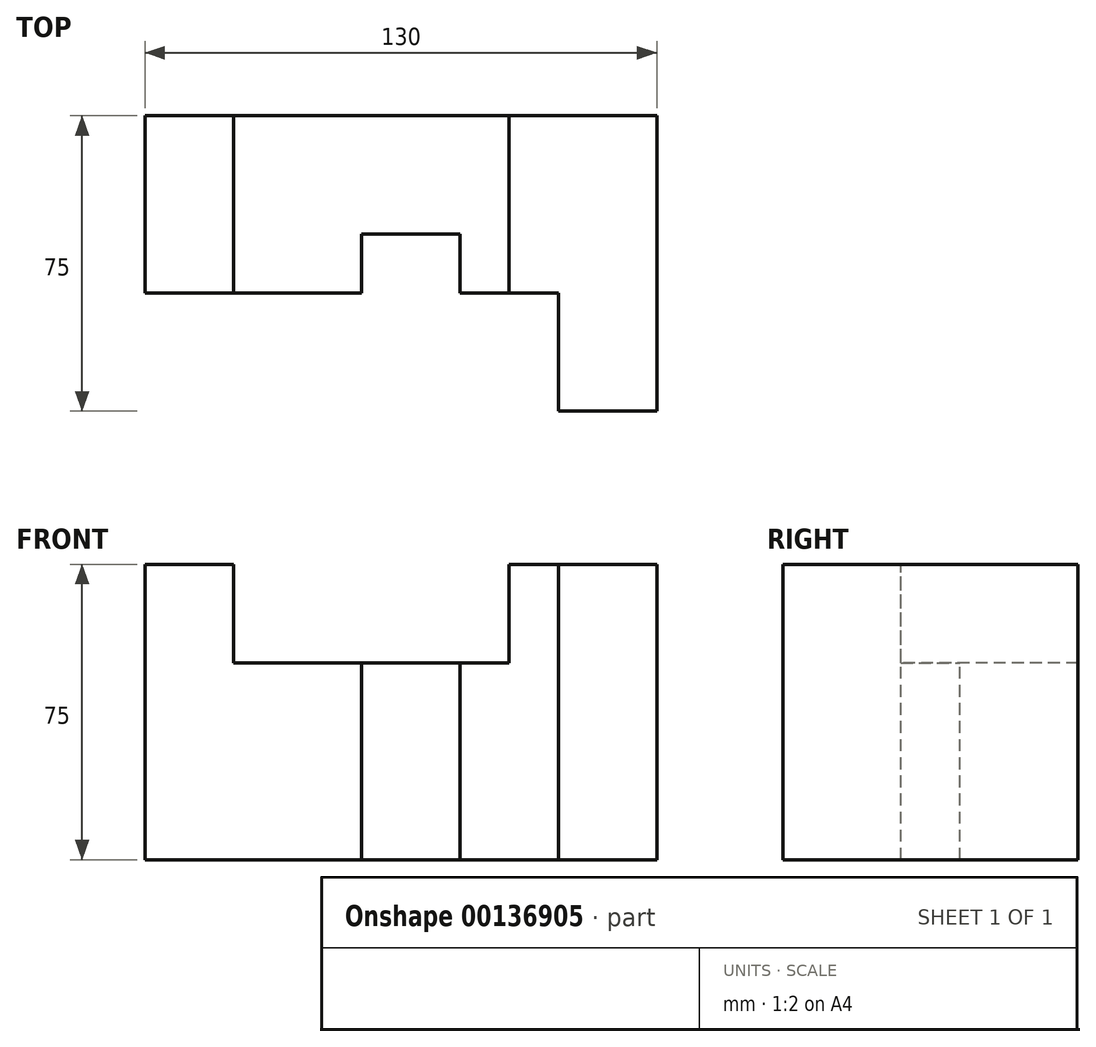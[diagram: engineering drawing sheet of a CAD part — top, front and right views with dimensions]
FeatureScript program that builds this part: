
annotation { "Feature Type Name" : "Feature", "Feature Type Description" : "" }
export const myFeature = defineFeature(function(context is Context, id is Id, definition is map)
    precondition{}
    {
        {
            var Q0;
            Q0=qCreatedBy(makeId("Top.planeOp"),FACE);
            var sketch = newSketch(context, id + "F0", { "sketchPlane" : qUnion([Q0])});
            skLineSegment(sketch, "E0", {"start": v(0, 0) * mm, "end": v(130, 0) * mm});
            skLineSegment(sketch, "E1", {"start": v(130, 0) * mm, "end": v(130, 75) * mm});
            skLineSegment(sketch, "E2", {"start": v(130, 75) * mm, "end": v(0, 75) * mm});
            skLineSegment(sketch, "E3", {"start": v(0, 75) * mm, "end": v(0, 0) * mm});
            skSolve(sketch);
        }
        {
            var Q0;
            Q0 = qSketchRegion(id + "F0", true);
            extrude(context, id + "F1", {"entities" : qUnion([Q0]), "depth" : 75 * mm});
        }
        {
            var Q0;
            Q0=makeQuery(id+"F1.opExtrude","CAP_FACE",FACE,{"disambiguationData":[OSD([sQuery(id+"F0.wireOp",EDGE,"E0"),sQuery(id+"F0.wireOp",EDGE,"E1"),sQuery(id+"F0.wireOp",EDGE,"E2"),sQuery(id+"F0.wireOp",EDGE,"E3")])],"isStart":false});
            var sketch = newSketch(context, id + "F2", { "sketchPlane" : qUnion([Q0])});
            skLineSegment(sketch, "E4", {"start": v(105, 0) * mm, "end": v(105, 30) * mm});
            skLineSegment(sketch, "E5", {"start": v(105, 30) * mm, "end": v(80, 30) * mm});
            skLineSegment(sketch, "E6", {"start": v(80, 30) * mm, "end": v(80, 45) * mm});
            skLineSegment(sketch, "E7", {"start": v(80, 45) * mm, "end": v(55, 45) * mm});
            skLineSegment(sketch, "E8", {"start": v(55, 45) * mm, "end": v(55, 30) * mm});
            skLineSegment(sketch, "E9", {"start": v(55, 30) * mm, "end": v(0, 30) * mm});
            skLineSegment(sketch, "E10", {"start": v(0, 30) * mm, "end": v(0, 0) * mm});
            skLineSegment(sketch, "E11", {"start": v(0, 0) * mm, "end": v(105, 0) * mm});
            skSolve(sketch);
        }
        {
            var Q0;
            Q0 = qSketchRegion(id + "F2", true);
            extrude(context, id + "F3", {"entities" : qUnion([Q0]), "operationType" : NewBodyOperationType.REMOVE, "oppositeDirection" : true, "depth" : 90 * mm});
        }
        {
            var Q0;
            Q0=makeQuery(id+"F1.opExtrude","CAP_FACE",FACE,{"disambiguationData":[OSD([sQuery(id+"F0.wireOp",EDGE,"E0"),sQuery(id+"F0.wireOp",EDGE,"E1"),sQuery(id+"F0.wireOp",EDGE,"E2"),sQuery(id+"F0.wireOp",EDGE,"E3")])],"isStart":false});
            var sketch = newSketch(context, id + "F4", { "sketchPlane" : qUnion([Q0])});
            skLineSegment(sketch, "E12", {"start": v(22.5, 75) * mm, "end": v(22.5, 30) * mm});
            skLineSegment(sketch, "E13", {"start": v(22.5, 30) * mm, "end": v(92.5, 30) * mm});
            skLineSegment(sketch, "E14", {"start": v(92.5, 30) * mm, "end": v(92.5, 75) * mm});
            skLineSegment(sketch, "E15", {"start": v(92.5, 75) * mm, "end": v(22.5, 75) * mm});
            skSolve(sketch);
        }
        {
            var Q0;
            {var subQ4=sQuery(id+"F4.wireOp",EDGE,"E12");Q0=makeQuery(id+"F4.imprint","IMPRINT",FACE,{"disambiguationData":[TD([[makeQuery(id+"F4.imprint","IMPRINT",EDGE,{"derivedFrom":subQ4}),1.0]])]});}
            extrude(context, id + "F5", {"entities" : qUnion([Q0]), "operationType" : NewBodyOperationType.REMOVE, "oppositeDirection" : true, "depth" : 25 * mm});
        }
    });
